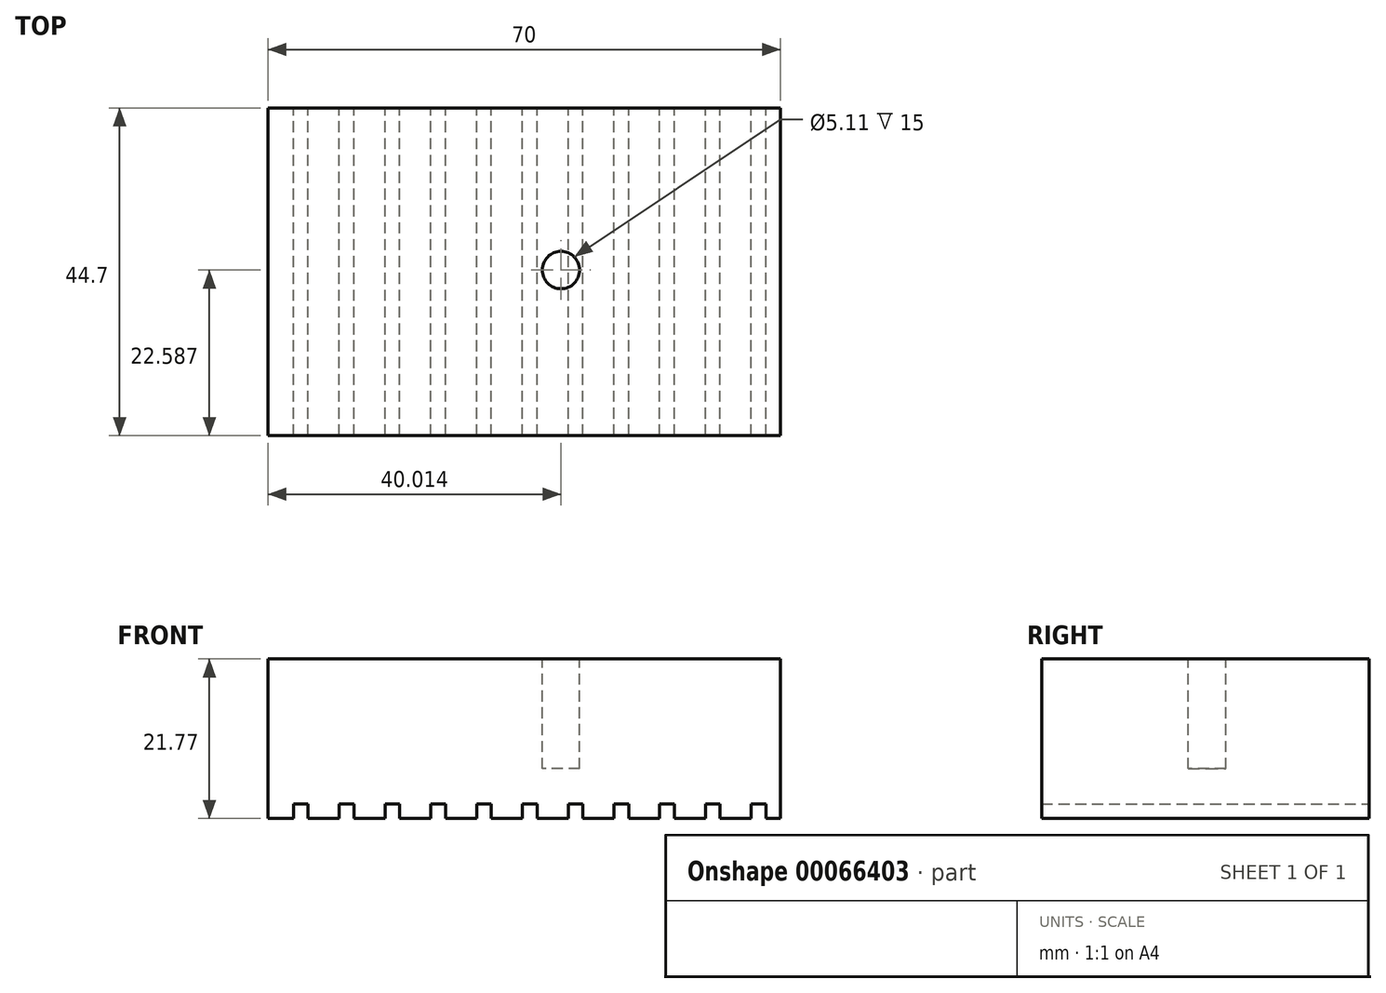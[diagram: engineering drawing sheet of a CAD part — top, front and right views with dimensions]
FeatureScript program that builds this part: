
annotation { "Feature Type Name" : "Feature", "Feature Type Description" : "" }
export const myFeature = defineFeature(function(context is Context, id is Id, definition is map)
    precondition{}
    {
        {
            var Q0;
            Q0=qCreatedBy(makeId("Top.planeOp"),FACE);
            var sketch = newSketch(context, id + "F0", { "sketchPlane" : qUnion([Q0])});
            skLineSegment(sketch, "E0.bottom", {"start": v(0, 0) * mm, "end": v(70, 0) * mm});
            skLineSegment(sketch, "E0.top", {"start": v(0, 44.7) * mm, "end": v(70, 44.7) * mm});
            skLineSegment(sketch, "E0.left", {"start": v(0, 0) * mm, "end": v(0, 44.7) * mm});
            skLineSegment(sketch, "E0.right", {"start": v(70, 0) * mm, "end": v(70, 44.7) * mm});
            skSolve(sketch);
        }
        {
            var Q0;
            Q0=makeQuery(id+"F0.imprint","IMPRINT",FACE,{"disambiguationData":[TD([[makeQuery(id+"F0.imprint","IMPRINT",EDGE,{"derivedFrom":sQuery(id+"F0.wireOp",EDGE,"E0.bottom")}),1.0]])]});
            extrude(context, id + "F1", {"entities" : qUnion([Q0]), "depth" : 21.77 * mm});
        }
        {
            var Q0;
            Q0=makeQuery(id+"F1.opExtrude","CAP_FACE",FACE,{"disambiguationData":[OSD([sQuery(id+"F0.wireOp",EDGE,"E0.bottom"),sQuery(id+"F0.wireOp",EDGE,"E0.top"),sQuery(id+"F0.wireOp",EDGE,"E0.left"),sQuery(id+"F0.wireOp",EDGE,"E0.right")])],"isStart":false});
            var sketch = newSketch(context, id + "F2", { "sketchPlane" : qUnion([Q0])});
            skCircle(sketch, "E1", {"center": v(40.01, 22.59) * mm, "radius": 2.55 * mm});
            skSolve(sketch);
        }
        {
            var Q0;
            Q0=makeQuery(id+"F2.imprint","IMPRINT",FACE,{"disambiguationData":[TD([[makeQuery(id+"F2.imprint","IMPRINT",EDGE,{"derivedFrom":sQuery(id+"F2.wireOp",EDGE,"E1")}),1.0]])]});
            extrude(context, id + "F3", {"entities" : qUnion([Q0]), "operationType" : NewBodyOperationType.REMOVE, "oppositeDirection" : true, "depth" : 15 * mm});
        }
        {
            var Q0;
            Q0=makeQuery(id+"F1.opExtrude","CAP_FACE",FACE,{"disambiguationData":[OSD([sQuery(id+"F0.wireOp",EDGE,"E0.bottom"),sQuery(id+"F0.wireOp",EDGE,"E0.top"),sQuery(id+"F0.wireOp",EDGE,"E0.left"),sQuery(id+"F0.wireOp",EDGE,"E0.right")])],"isStart":true});
            var sketch = newSketch(context, id + "F4", { "sketchPlane" : qUnion([Q0])});
            skLineSegment(sketch, "E2.bottom", {"start": v(68, 0) * mm, "end": v(66, 0) * mm});
            skLineSegment(sketch, "E2.top", {"start": v(68, -44.7) * mm, "end": v(66, -44.7) * mm});
            skLineSegment(sketch, "E2.left", {"start": v(68, 0) * mm, "end": v(68, -44.7) * mm});
            skLineSegment(sketch, "E2.right", {"start": v(66, 0) * mm, "end": v(66, -44.7) * mm});
            skLineSegment(sketch, "E3.1.0.0", {"start": v(61.75, -44.7) * mm, "end": v(59.75, -44.7) * mm});
            skLineSegment(sketch, "E3.1.0.1", {"start": v(59.75, 0) * mm, "end": v(59.75, -44.7) * mm});
            skLineSegment(sketch, "E3.1.0.2", {"start": v(61.75, 0) * mm, "end": v(61.75, -44.7) * mm});
            skLineSegment(sketch, "E3.1.0.3", {"start": v(61.75, 0) * mm, "end": v(59.75, 0) * mm});
            skLineSegment(sketch, "E3.2.0.0", {"start": v(55.5, -44.7) * mm, "end": v(53.5, -44.7) * mm});
            skLineSegment(sketch, "E3.2.0.1", {"start": v(53.5, 0) * mm, "end": v(53.5, -44.7) * mm});
            skLineSegment(sketch, "E3.2.0.2", {"start": v(55.5, 0) * mm, "end": v(55.5, -44.7) * mm});
            skLineSegment(sketch, "E3.2.0.3", {"start": v(55.5, 0) * mm, "end": v(53.5, 0) * mm});
            skLineSegment(sketch, "E3.3.0.0", {"start": v(49.25, -44.7) * mm, "end": v(47.25, -44.7) * mm});
            skLineSegment(sketch, "E3.3.0.1", {"start": v(47.25, 0) * mm, "end": v(47.25, -44.7) * mm});
            skLineSegment(sketch, "E3.3.0.2", {"start": v(49.25, 0) * mm, "end": v(49.25, -44.7) * mm});
            skLineSegment(sketch, "E3.3.0.3", {"start": v(49.25, 0) * mm, "end": v(47.25, 0) * mm});
            skLineSegment(sketch, "E3.4.0.0", {"start": v(43, -44.7) * mm, "end": v(41, -44.7) * mm});
            skLineSegment(sketch, "E3.4.0.1", {"start": v(41, 0) * mm, "end": v(41, -44.7) * mm});
            skLineSegment(sketch, "E3.4.0.2", {"start": v(43, 0) * mm, "end": v(43, -44.7) * mm});
            skLineSegment(sketch, "E3.4.0.3", {"start": v(43, 0) * mm, "end": v(41, 0) * mm});
            skLineSegment(sketch, "E3.5.0.0", {"start": v(36.75, -44.7) * mm, "end": v(34.75, -44.7) * mm});
            skLineSegment(sketch, "E3.5.0.1", {"start": v(34.75, 0) * mm, "end": v(34.75, -44.7) * mm});
            skLineSegment(sketch, "E3.5.0.2", {"start": v(36.75, 0) * mm, "end": v(36.75, -44.7) * mm});
            skLineSegment(sketch, "E3.5.0.3", {"start": v(36.75, 0) * mm, "end": v(34.75, 0) * mm});
            skLineSegment(sketch, "E3.6.0.0", {"start": v(30.5, -44.7) * mm, "end": v(28.5, -44.7) * mm});
            skLineSegment(sketch, "E3.6.0.1", {"start": v(28.5, 0) * mm, "end": v(28.5, -44.7) * mm});
            skLineSegment(sketch, "E3.6.0.2", {"start": v(30.5, 0) * mm, "end": v(30.5, -44.7) * mm});
            skLineSegment(sketch, "E3.6.0.3", {"start": v(30.5, 0) * mm, "end": v(28.5, 0) * mm});
            skLineSegment(sketch, "E3.7.0.0", {"start": v(24.25, -44.7) * mm, "end": v(22.25, -44.7) * mm});
            skLineSegment(sketch, "E3.7.0.1", {"start": v(22.25, 0) * mm, "end": v(22.25, -44.7) * mm});
            skLineSegment(sketch, "E3.7.0.2", {"start": v(24.25, 0) * mm, "end": v(24.25, -44.7) * mm});
            skLineSegment(sketch, "E3.7.0.3", {"start": v(24.25, 0) * mm, "end": v(22.25, 0) * mm});
            skLineSegment(sketch, "E3.8.0.0", {"start": v(18, -44.7) * mm, "end": v(16, -44.7) * mm});
            skLineSegment(sketch, "E3.8.0.1", {"start": v(16, 0) * mm, "end": v(16, -44.7) * mm});
            skLineSegment(sketch, "E3.8.0.2", {"start": v(18, 0) * mm, "end": v(18, -44.7) * mm});
            skLineSegment(sketch, "E3.8.0.3", {"start": v(18, 0) * mm, "end": v(16, 0) * mm});
            skLineSegment(sketch, "E3.9.0.0", {"start": v(11.75, -44.7) * mm, "end": v(9.75, -44.7) * mm});
            skLineSegment(sketch, "E3.9.0.1", {"start": v(9.75, 0) * mm, "end": v(9.75, -44.7) * mm});
            skLineSegment(sketch, "E3.9.0.2", {"start": v(11.75, 0) * mm, "end": v(11.75, -44.7) * mm});
            skLineSegment(sketch, "E3.9.0.3", {"start": v(11.75, 0) * mm, "end": v(9.75, 0) * mm});
            skLineSegment(sketch, "E3.10.0.0", {"start": v(5.5, -44.7) * mm, "end": v(3.5, -44.7) * mm});
            skLineSegment(sketch, "E3.10.0.1", {"start": v(3.5, 0) * mm, "end": v(3.5, -44.7) * mm});
            skLineSegment(sketch, "E3.10.0.2", {"start": v(5.5, 0) * mm, "end": v(5.5, -44.7) * mm});
            skLineSegment(sketch, "E3.10.0.3", {"start": v(5.5, 0) * mm, "end": v(3.5, 0) * mm});
            skLineSegment(sketch, "E3.11.0.0", {"start": v(-0.75, -44.7) * mm, "end": v(-2.75, -44.7) * mm});
            skLineSegment(sketch, "E3.11.0.1", {"start": v(-2.75, 0) * mm, "end": v(-2.75, -44.7) * mm});
            skLineSegment(sketch, "E3.11.0.2", {"start": v(-0.75, 0) * mm, "end": v(-0.75, -44.7) * mm});
            skLineSegment(sketch, "E3.11.0.3", {"start": v(-0.75, 0) * mm, "end": v(-2.75, 0) * mm});
            skLineSegment(sketch, "E3.direction1", {"start": v(66, -44.7) * mm, "end": v(59.75, -44.7) * mm, "construction": true});
            skSolve(sketch);
        }
        {
            var Q0;
            Q0 = qSketchRegion(id + "F4", true);
            extrude(context, id + "F5", {"entities" : qUnion([Q0]), "operationType" : NewBodyOperationType.REMOVE, "oppositeDirection" : true, "depth" : 2 * mm});
        }
    });
